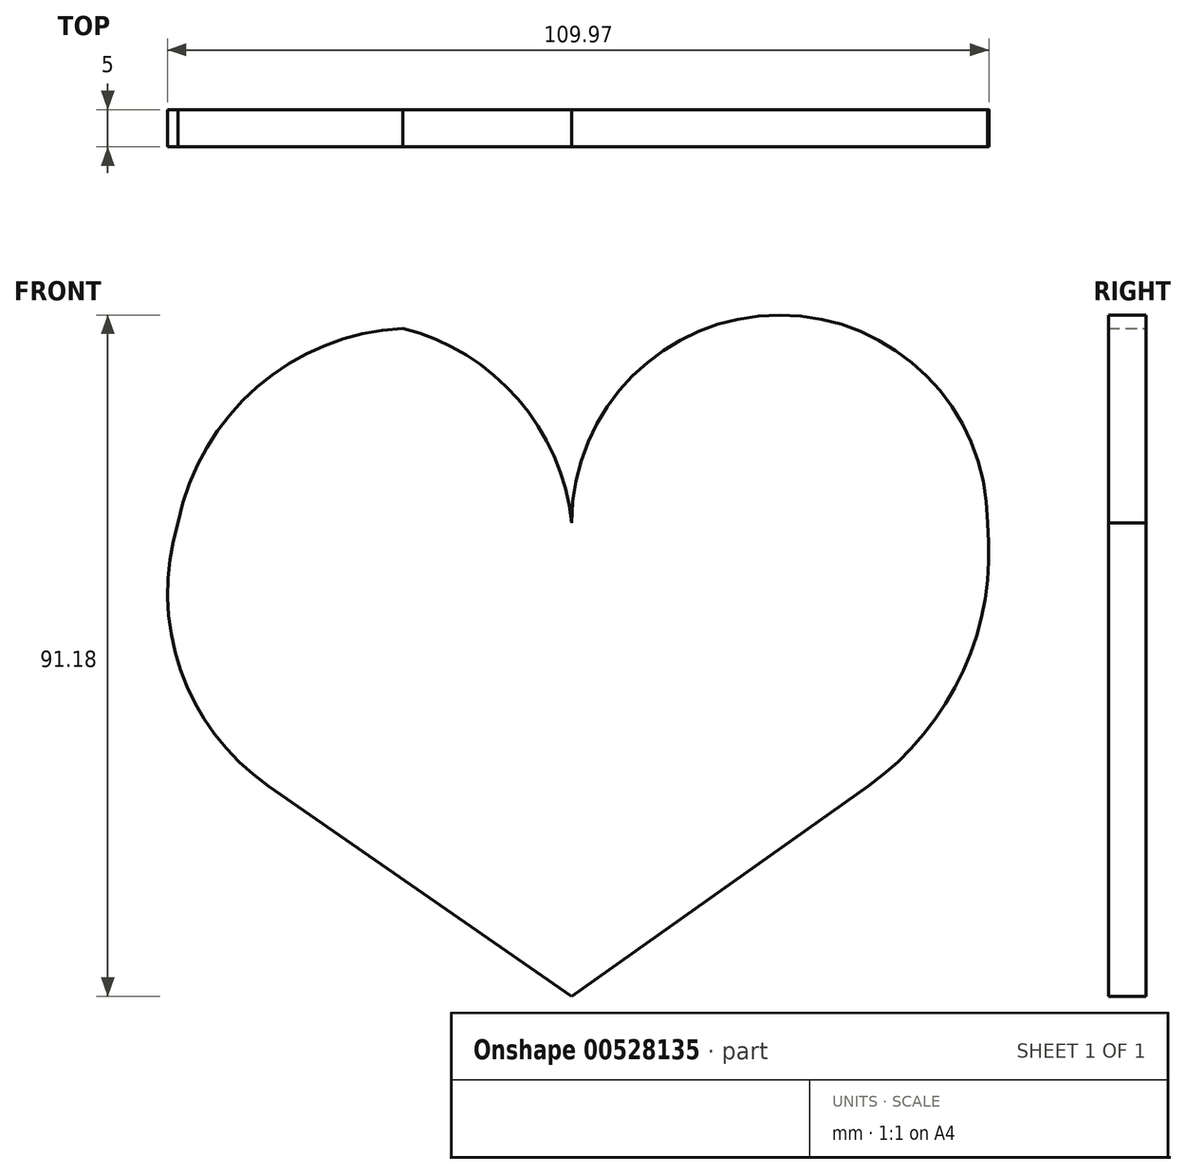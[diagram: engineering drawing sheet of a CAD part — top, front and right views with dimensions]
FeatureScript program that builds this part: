
annotation { "Feature Type Name" : "Feature", "Feature Type Description" : "" }
export const myFeature = defineFeature(function(context is Context, id is Id, definition is map)
    precondition{}
    {
        {
            var Q0;
            Q0=qCreatedBy(makeId("Front.planeOp"),FACE);
            var sketch = newSketch(context, id + "F0", { "sketchPlane" : qUnion([Q0])});
            skArc(sketch, "E0", {"start": v(55.66, 0) * mm, "mid": v(27.83, 27.83) * mm, "end": v(0, 0) * mm});
            skArc(sketch, "E1", {"start": v(39.67, -35.23) * mm, "mid": v(52.43, -19.78) * mm, "end": v(55.66, 0) * mm});
            skLineSegment(sketch, "E2", {"start": v(39.67, -35.23) * mm, "end": v(0, -63.35) * mm});
            skLineSegment(sketch, "E3", {"start": v(0, -63.35) * mm, "end": v(-40.56, -35.23) * mm});
            skArc(sketch, "E4", {"start": v(-52.7, 0) * mm, "mid": v(-52.4, -19.6) * mm, "end": v(-40.56, -35.23) * mm});
            skArc(sketch, "E5", {"start": v(0, 0) * mm, "mid": v(-7.2, 16.59) * mm, "end": v(-22.6, 26.05) * mm});
            skArc(sketch, "E6", {"start": v(-22.6, 26.05) * mm, "mid": v(-42.12, 18.2) * mm, "end": v(-52.7, 0) * mm});
            skSolve(sketch);
        }
        {
            var Q0;
            Q0=makeQuery(id+"F0.imprint","IMPRINT",FACE,{"disambiguationData":[TD([[makeQuery(id+"F0.imprint","IMPRINT",EDGE,{"derivedFrom":sQuery(id+"F0.wireOp",EDGE,"E0")}),1.0]])]});
            extrude(context, id + "F1", {"entities" : qUnion([Q0]), "depth" : 5 * mm, "offsetDistance" : 25 * mm});
        }
    });
